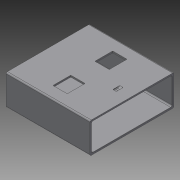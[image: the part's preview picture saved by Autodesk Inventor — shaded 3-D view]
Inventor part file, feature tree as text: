
AUTODESK INVENTOR PART (.ipt)
format: ipt  version: 2015 (Build 190159000, 159)  size: 298,496 bytes
history: native  units: mm
features: extrude x5, fillet x5, sketch x5, mirror x1
ambient origin geometry x8: Origin, YZ Plane, XZ Plane, XY Plane, X Axis, Y Axis, Z Axis, Center Point
bodies: Solid1 (feature_tree)
feature tree (16):
  extrude  "Extrusion1"  Depth=12.192mm
  extrude  "Extrusion2"  Depth=6.096mm
  extrude  "Extrusion3"  Depth=0.254mm
  mirror  "Mirror1"
  extrude  "Extrusion4"  Depth=0.254mm
  extrude  "Extrusion5"  TaperAngle=0.0deg  [1 undecoded]
  fillet  "Fillet1"  Radius=5.08mm
  fillet  "Fillet2"  Radius=1.778mm
  fillet  "Fillet3"  Radius=2.54mm
  fillet  "Fillet4"  Radius=2.032mm
  fillet  "Fillet5"  [1 undecoded]
  sketch  "Sketch2"  dims[d4=12.192mm d5=12.192mm]
  sketch  "Sketch3"  dims[d6=6.096mm d7=6.096mm]
  sketch  "Sketch4"  dims[d8=4.445mm d9=0.0mm d10=0.254mm]
  sketch  "Sketch5"  dims[d11=0.254mm d12=0.254mm]
  sketch  "Sketch6"  dims[d13=0.254mm d14=0.0mm d15=0.0mm d16=5.08mm d17=1.778mm d18=2.54mm d19=2.032mm d20=0.0mm d21=0.0mm d22=0.0762mm d23=0.0762mm d25=0.0762mm d26=0.254mm d27=0.0127mm d28=1.524mm d29=1.397mm d30=1.778mm d31=0.003175mm d32=0.0mm d33=5.588mm d34=1.778mm d35=0.508mm d36=1.016mm d37=0.127mm d38=0.0mm d39=0.635mm d40=0.0635mm d41=0.1905mm d42=0.03175mm d43=0.03175mm]
note: 2 required parameter values undecoded (feature->parameter linkage not recoverable at this tier; creation-order binding heuristic only, values carry confidence <= 0.55)
